# Revit family: Toilet-Floor_Mount-KOHLER-EIR-K-77798T_1
name_source: partatom
category: Plumbing Fixtures
revit_build: Autodesk Revit 2017 (Build: 20160225_1515(x64)
units: mm (PartAtom-declared; Revit-internal decimal feet)

## family parameters
Cut with Voids When Loaded = No
Host = Face
OmniClass Number = 23.31.19.00
Part Type = Normal
Room Calculation Point = No
Round Connector Dimension = Use Diameter
Shared = No

## types (2) — shared parameters
ADA Compliant = No
Apparent Load = 2200 VA
Assembly Code = D2010100
CW Connection = Yes
Cold Water Inlet = Cold Water Inlet
Date Modified = 05/11/2021
Default Elevation = 0"
Description = Shangsi Smart Toilet
Electrical Connector = Yes
Electrical Note = One dedicated circuit required
Finish = Kohler-Vitreous_China-0-White
Flow Rate = 0 GPM
Flush Rate- GPF = 1.0GPF
Flush Rate- LPF = 3.8LPF
HW Connection = No
Height = 20 9/16"
Hot Water Inlet = Hot Water Inlet
Length = 27 9/16"
Manufacturer = KOHLER Co.
Master Format 2014 = 22 41 13.13
Master Format 2014 Name = Residential Water Closets
Material = Vitreous China
Pressure = 107.33 psi
Product Documentation Link = https://files.kohler.com.cn
Product Name = Eir
Product Page URL = https://www.kohler.com.cn
Rough-In = 12"
Seat Included = Yes
URL = http://www.kohler.com.cn
Vent Connection = No
Voltage = 220 V
Waste Connection = Yes
Waste Water Outlet = Waste Water Outlet
WaterSense Certified = No
Width = 16 7/16"

## per-type parameters (varying)
| type | Model | Type |
| 0- White | K-77798T-0 | 1 |
| EX-0-White | K-77798T-EX-0 | 2 |

## geometry (parser evidence)
native form markers: Sweep x5
no freeform markers — native parametric forms only
